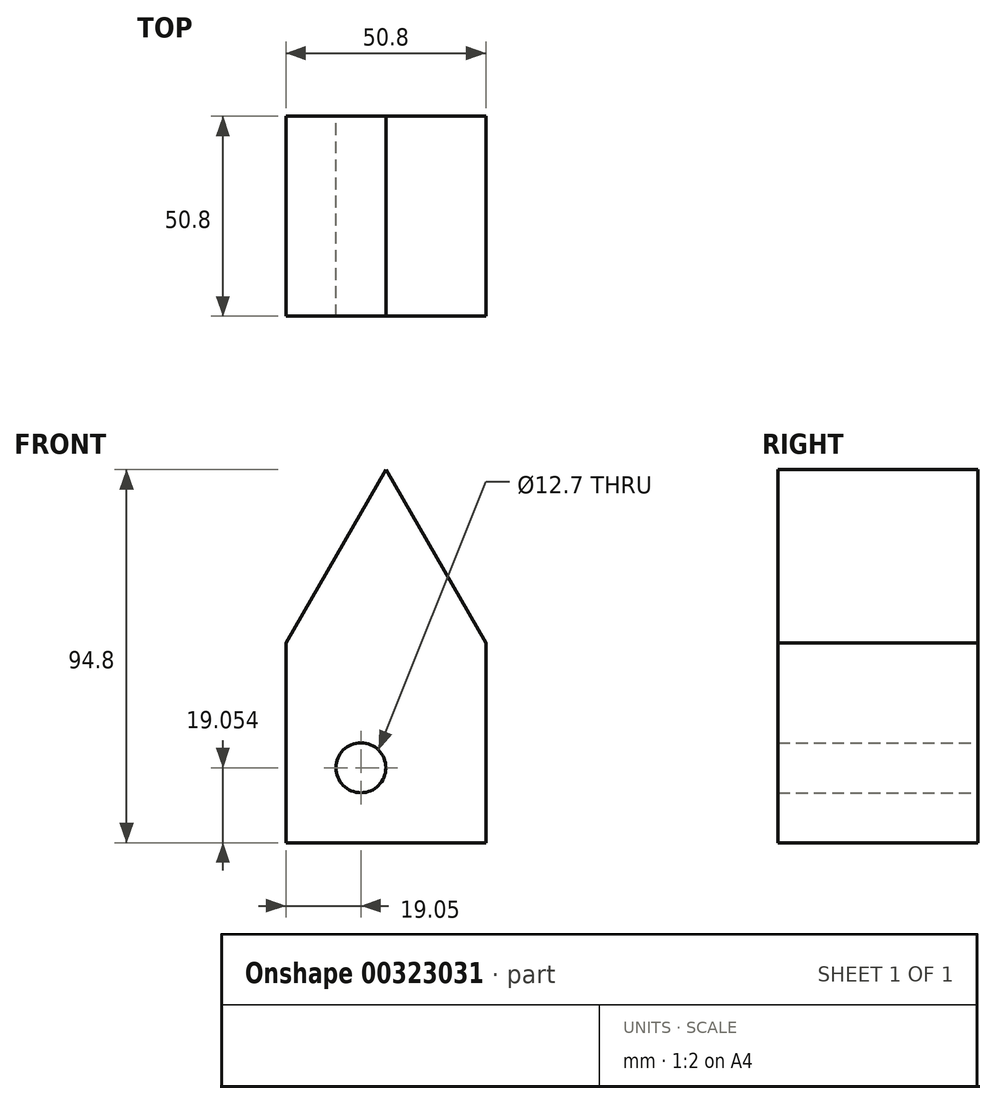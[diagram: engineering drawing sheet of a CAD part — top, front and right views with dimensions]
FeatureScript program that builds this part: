
annotation { "Feature Type Name" : "Feature", "Feature Type Description" : "" }
export const myFeature = defineFeature(function(context is Context, id is Id, definition is map)
    precondition{}
    {
        {
            var Q0;
            Q0=qCreatedBy(makeId("Front.planeOp"),FACE);
            var sketch = newSketch(context, id + "F0", { "sketchPlane" : qUnion([Q0])});
            skLineSegment(sketch, "E0.top", {"start": v(-25.4, -47.13) * mm, "end": v(25.4, -47.13) * mm});
            skLineSegment(sketch, "E0.left", {"start": v(-25.4, 3.67) * mm, "end": v(-25.4, -47.13) * mm});
            skLineSegment(sketch, "E0.right", {"start": v(25.4, 3.67) * mm, "end": v(25.4, -47.13) * mm});
            skLineSegment(sketch, "E1", {"start": v(-25.4, 3.67) * mm, "end": v(0, 47.67) * mm});
            skLineSegment(sketch, "E2", {"start": v(25.4, 3.67) * mm, "end": v(0, 47.67) * mm});
            skCircle(sketch, "E3", {"center": v(-6.35, -28.08) * mm, "radius": 6.35 * mm});
            skSolve(sketch);
        }
        {
            var Q0;
            Q0=makeQuery(id+"F0.imprint","IMPRINT",FACE,{"disambiguationData":[TD([[makeQuery(id+"F0.imprint","IMPRINT",EDGE,{"derivedFrom":sQuery(id+"F0.wireOp",EDGE,"E0.top")}),1.0]])]});
            extrude(context, id + "F1", {"entities" : qUnion([Q0]), "depth" : 50.8 * mm});
        }
    });
